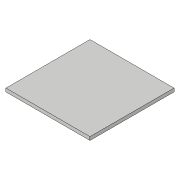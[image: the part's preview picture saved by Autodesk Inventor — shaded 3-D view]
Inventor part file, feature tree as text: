
AUTODESK INVENTOR PART (.ipt)
format: ipt  version: 2018.3 (Build 223284000, 284)  size: 73,216 bytes
history: native  units: in
note: dims shown in document units (in); Inventor stores cm internally (conversion verified against a paired STEP export)
features: extrude x1, sketch x1
ambient origin geometry x8: Origin, YZ Plane, XZ Plane, XY Plane, X Axis, Y Axis, Z Axis, Center Point
bodies: Solid1 (feature_tree)
feature tree (2):
  extrude  "Extrusion1"  Depth=3.125in
  sketch  "Sketch1"  dims[d0=3.125in d1=3.125in d2=0.125in d3=0.0in]
